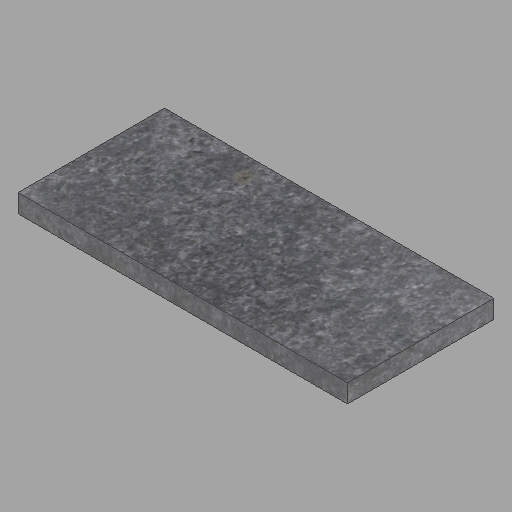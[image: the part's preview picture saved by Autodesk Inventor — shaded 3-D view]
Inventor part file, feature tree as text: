
AUTODESK INVENTOR PART (.ipt)
format: ipt  version: 2023 (Build 270158000, 158)  size: 225,792 bytes
history: native  units: in
note: dims shown in document units (in); Inventor stores cm internally (conversion verified against a paired STEP export)
features: other x1, extrude x1, sketch x1
ambient origin geometry x8: Origin, YZ Plane, XZ Plane, XY Plane, X Axis, Y Axis, Z Axis, Center Point
bodies: Solid1 (feature_tree)
feature tree (3):
  other  "2x16x36-3"
  extrude  "Extrusion1"  Depth=2.0in
  sketch  "Sketch1"  dims[d0=16.0in d1=2.0in d2=36.0in d3=0.0in]
